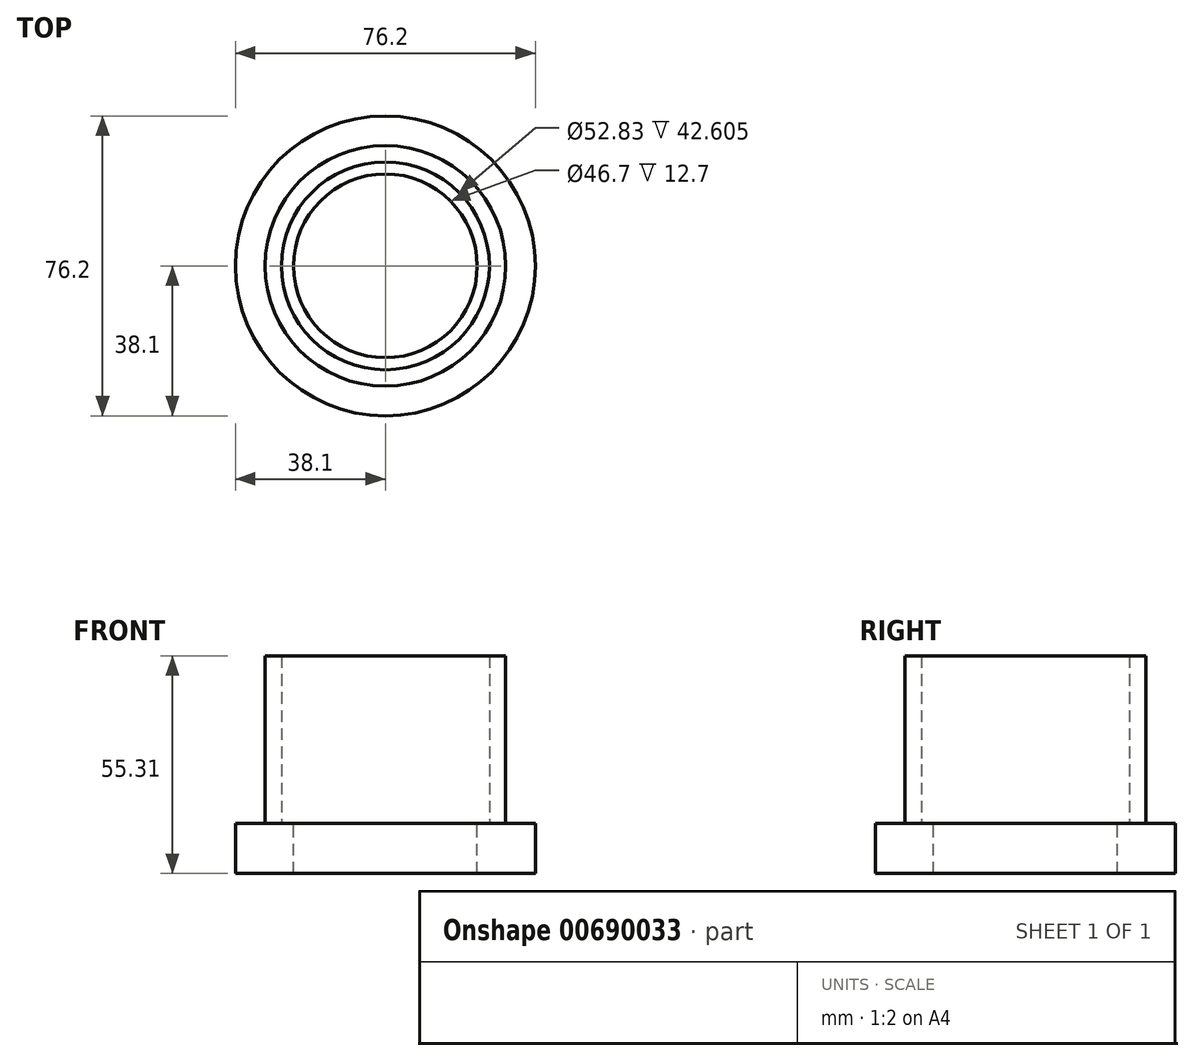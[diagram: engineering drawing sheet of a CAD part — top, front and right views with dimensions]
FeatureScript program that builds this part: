
annotation { "Feature Type Name" : "Feature", "Feature Type Description" : "" }
export const myFeature = defineFeature(function(context is Context, id is Id, definition is map)
    precondition{}
    {
        {
            var Q0;
            Q0=qCreatedBy(makeId("Top.planeOp"),FACE);
            cPlane(context, id + "F0", {"entities" : qUnion([Q0]), "cplaneType" : CPlaneType.OFFSET, "offset" : 64.26 * mm, "oppositeDirection" : true, "width" : 152.4 * mm, "height" : 152.4 * mm});
        }
        {
            var Q0;
            Q0=qCreatedBy(id+"F0.planeOp",FACE);
            var sketch = newSketch(context, id + "F1", { "sketchPlane" : qUnion([Q0])});
            skCircle(sketch, "E0", {"center": v(0, 0) * mm, "radius": 30.58 * mm});
            skCircle(sketch, "E1", {"center": v(0, 0) * mm, "radius": 26.41 * mm});
            skSolve(sketch);
        }
        {
            var Q0;
            Q0=makeQuery(id+"F1.imprint","IMPRINT",FACE,{"disambiguationData":[TD([[makeQuery(id+"F1.imprint","IMPRINT",EDGE,{"derivedFrom":sQuery(id+"F1.wireOp",EDGE,"E0")}),1.0]])]});
            extrude(context, id + "F2", {"entities" : qUnion([Q0]), "depth" : 42.6 * mm, "offsetDistance" : 25.4 * mm});
        }
        {
            var Q0;
            Q0=qCreatedBy(id+"F0.planeOp",FACE);
            var sketch = newSketch(context, id + "F3", { "sketchPlane" : qUnion([Q0])});
            skCircle(sketch, "E2", {"center": v(0, 0) * mm, "radius": 38.1 * mm});
            skSolve(sketch);
        }
        {
            var Q0;
            Q0=makeQuery(id+"F3.imprint","IMPRINT",FACE,{"disambiguationData":[TD([[makeQuery(id+"F3.imprint","IMPRINT",EDGE,{"derivedFrom":sQuery(id+"F3.wireOp",EDGE,"E2")}),1.0]])]});
            extrude(context, id + "F4", {"entities" : qUnion([Q0]), "operationType" : NewBodyOperationType.ADD, "oppositeDirection" : true, "depth" : 12.7 * mm, "offsetDistance" : 25.4 * mm});
        }
        {
            var Q0;
            Q0=makeQuery(id+"F4.boolean.opBoolean","SPLIT",FACE,{"disambiguationData":[TD([makeQuery(id+"F2.opExtrude","SWEPT_FACE",FACE,{"disambiguationData":[OSD([sQuery(id+"F1.wireOp",EDGE,"E1")])]})])],"derivedFrom":makeQuery(id+"F4.opExtrude","CAP_FACE",FACE,{"disambiguationData":[OSD([sQuery(id+"F3.wireOp",EDGE,"E2")])],"isStart":true})});
            var sketch = newSketch(context, id + "F5", { "sketchPlane" : qUnion([Q0])});
            skCircle(sketch, "E3", {"center": v(0, 0) * mm, "radius": 23.35 * mm});
            skSolve(sketch);
        }
        {
            var Q0;
            Q0=makeQuery(id+"F5.imprint","IMPRINT",FACE,{"disambiguationData":[TD([[makeQuery(id+"F5.imprint","IMPRINT",EDGE,{"derivedFrom":sQuery(id+"F5.wireOp",EDGE,"E3")}),1.0]])]});
            extrude(context, id + "F6", {"entities" : qUnion([Q0]), "operationType" : NewBodyOperationType.REMOVE, "oppositeDirection" : true, "depth" : 25.4 * mm, "offsetDistance" : 25.4 * mm});
        }
    });
